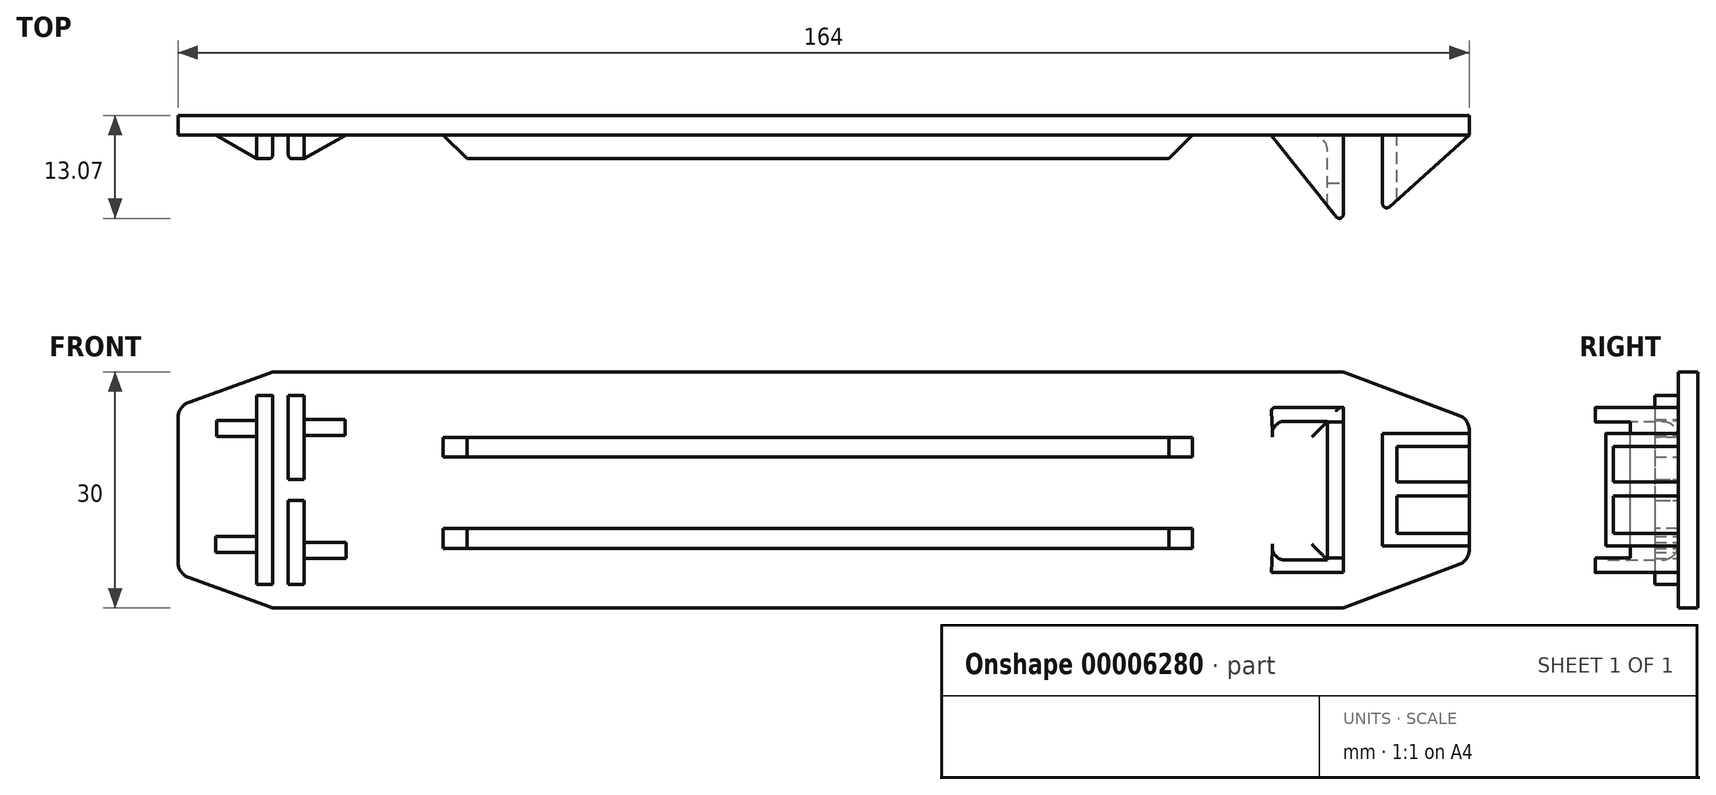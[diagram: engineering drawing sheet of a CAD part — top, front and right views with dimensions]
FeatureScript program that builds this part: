
annotation { "Feature Type Name" : "Feature", "Feature Type Description" : "" }
export const myFeature = defineFeature(function(context is Context, id is Id, definition is map)
    precondition{}
    {
        {
            var Q0;
            Q0=qCreatedBy(makeId("Front.planeOp"),FACE);
            var sketch = newSketch(context, id + "F0", { "sketchPlane" : qUnion([Q0])});
            skLineSegment(sketch, "E0.rect.bottom", {"start": v(66, -15) * mm, "end": v(-70, -15) * mm});
            skLineSegment(sketch, "E0.rect.top", {"start": v(66, 15) * mm, "end": v(-70, 15) * mm});
            skLineSegment(sketch, "E0.rect.left", {"start": v(82, -9) * mm, "end": v(82, 9) * mm});
            skLineSegment(sketch, "E0.rect.right", {"start": v(-82, -10.63) * mm, "end": v(-82, 10.63) * mm});
            skPoint(sketch, "E0.rect.middle", {"position": v(0, 0) * mm});
            skLineSegment(sketch, "E1", {"start": v(66, 15) * mm, "end": v(66, -9.93) * mm, "construction": true});
            skLineSegment(sketch, "E2.rect.bottom", {"start": v(77.85, 9) * mm, "end": v(71, 9) * mm, "construction": true});
            skLineSegment(sketch, "E2.rect.top", {"start": v(77.85, -9) * mm, "end": v(71, -9) * mm, "construction": true});
            skLineSegment(sketch, "E2.rect.left", {"start": v(82, 9) * mm, "end": v(82, -9) * mm, "construction": true});
            skLineSegment(sketch, "E2.rect.right", {"start": v(71, 9) * mm, "end": v(71, -9) * mm, "construction": true});
            skPoint(sketch, "E2.rect.middle", {"position": v(76.5, 0) * mm});
            skLineSegment(sketch, "E3", {"start": v(82, 9) * mm, "end": v(66, 15) * mm});
            skLineSegment(sketch, "E4", {"start": v(82, -9) * mm, "end": v(66, -15) * mm});
            skPoint(sketch, "E5.orphan", {"position": v(82, 15) * mm});
            skPoint(sketch, "E6.orphan", {"position": v(82, -15) * mm});
            skLineSegment(sketch, "E7.rect.bottom", {"start": v(66, 10.5) * mm, "end": v(77.85, 10.5) * mm, "construction": true});
            skLineSegment(sketch, "E7.rect.top", {"start": v(66, -10.5) * mm, "end": v(77.85, -10.5) * mm, "construction": true});
            skLineSegment(sketch, "E7.rect.left", {"start": v(66, 10.5) * mm, "end": v(66, -10.5) * mm, "construction": true});
            skLineSegment(sketch, "E7.rect.right", {"start": v(77.85, 10.5) * mm, "end": v(77.85, -10.5) * mm, "construction": true});
            skPoint(sketch, "E7.rect.middle", {"position": v(71.92, 0) * mm});
            skLineSegment(sketch, "E8.bottom", {"start": v(66, 10.5) * mm, "end": v(56.87, 10.5) * mm});
            skLineSegment(sketch, "E8.top", {"start": v(66, -10.5) * mm, "end": v(56.87, -10.5) * mm});
            skLineSegment(sketch, "E8.left", {"start": v(66, 10.5) * mm, "end": v(66, -10.5) * mm});
            skLineSegment(sketch, "E9.bottom", {"start": v(64, 8.72) * mm, "end": v(56.94, 8.72) * mm});
            skLineSegment(sketch, "E9.top", {"start": v(64, -8.88) * mm, "end": v(56.94, -8.88) * mm});
            skLineSegment(sketch, "E9.left", {"start": v(66, 8.72) * mm, "end": v(66, -8.88) * mm});
            skLineSegment(sketch, "E10", {"start": v(56.87, 10.5) * mm, "end": v(56.94, 8.72) * mm});
            skLineSegment(sketch, "E11", {"start": v(56.94, -8.88) * mm, "end": v(56.87, -10.5) * mm});
            skLineSegment(sketch, "E12", {"start": v(64, 8.72) * mm, "end": v(64, -8.88) * mm});
            skLineSegment(sketch, "E13", {"start": v(71, -9) * mm, "end": v(71, 9) * mm});
            skLineSegment(sketch, "E14", {"start": v(71, 7.5) * mm, "end": v(77.85, 7.5) * mm});
            skLineSegment(sketch, "E15", {"start": v(71, -7.5) * mm, "end": v(77.85, -7.5) * mm});
            skLineSegment(sketch, "E16.bottom", {"start": v(72.8, 5.5) * mm, "end": v(82, 5.5) * mm});
            skLineSegment(sketch, "E16.top", {"start": v(72.8, -5.5) * mm, "end": v(82, -5.5) * mm});
            skLineSegment(sketch, "E16.left", {"start": v(72.8, 5.5) * mm, "end": v(72.8, 1.01) * mm});
            skLineSegment(sketch, "E16.right", {"start": v(82, 5.5) * mm, "end": v(82, -5.5) * mm});
            skLineSegment(sketch, "E17.bottom", {"start": v(72.8, 1.01) * mm, "end": v(82, 1.01) * mm});
            skLineSegment(sketch, "E17.top", {"start": v(72.8, -0.79) * mm, "end": v(82, -0.79) * mm});
            skLineSegment(sketch, "E17.right", {"start": v(82, 1.01) * mm, "end": v(82, -0.79) * mm});
            skLineSegment(sketch, "E18.trimOffspring", {"start": v(72.8, -0.79) * mm, "end": v(72.8, -5.5) * mm});
            skLineSegment(sketch, "E19", {"start": v(71, 7.15) * mm, "end": v(82, 7.15) * mm});
            skLineSegment(sketch, "E20", {"start": v(71, -7.11) * mm, "end": v(82, -7.11) * mm});
            skLineSegment(sketch, "E21", {"start": v(82, -7.11) * mm, "end": v(81.8, -7.11) * mm});
            skLineSegment(sketch, "E22", {"start": v(-70, 3.24) * mm, "end": v(-70, -5.11) * mm, "construction": true});
            skLineSegment(sketch, "E23.rect.bottom", {"start": v(-70, 10.63) * mm, "end": v(-82, 10.63) * mm, "construction": true});
            skLineSegment(sketch, "E23.rect.top", {"start": v(-70, -10.63) * mm, "end": v(-82, -10.63) * mm, "construction": true});
            skLineSegment(sketch, "E23.rect.left", {"start": v(-70, 15) * mm, "end": v(-70, -15) * mm, "construction": true});
            skLineSegment(sketch, "E23.rect.right", {"start": v(-81.6, 10.63) * mm, "end": v(-81.6, -10.63) * mm, "construction": true});
            skPoint(sketch, "E23.rect.middle", {"position": v(-75.8, 0) * mm});
            skLineSegment(sketch, "E24", {"start": v(-82, 10.63) * mm, "end": v(-70, 15) * mm});
            skLineSegment(sketch, "E25", {"start": v(-70, -15) * mm, "end": v(-82, -10.63) * mm});
            skPoint(sketch, "E26.orphan", {"position": v(-82, 15) * mm});
            skPoint(sketch, "E27.orphan", {"position": v(-82, -15) * mm});
            skLineSegment(sketch, "E28.rect.bottom", {"start": v(-70, 12) * mm, "end": v(-72, 12) * mm});
            skLineSegment(sketch, "E28.rect.top", {"start": v(-70, -12) * mm, "end": v(-72, -12) * mm});
            skLineSegment(sketch, "E28.rect.right", {"start": v(-72, 12) * mm, "end": v(-72, -12) * mm});
            skPoint(sketch, "E28.rect.middle", {"position": v(-70, 0) * mm});
            skPoint(sketch, "E28.rect.left.start.orphan", {"position": v(-68, 12) * mm});
            skPoint(sketch, "E29.orphan", {"position": v(-68, -12) * mm});
            skLineSegment(sketch, "E30", {"start": v(-70, 12) * mm, "end": v(-70, -12) * mm});
            skLineSegment(sketch, "E31.rect.bottom", {"start": v(-66, 12) * mm, "end": v(-68, 12) * mm});
            skLineSegment(sketch, "E31.rect.top", {"start": v(-66, -12) * mm, "end": v(-68, -12) * mm});
            skLineSegment(sketch, "E31.rect.left", {"start": v(-66, 12) * mm, "end": v(-66, 1.35) * mm});
            skLineSegment(sketch, "E31.rect.right", {"start": v(-68, 12) * mm, "end": v(-68, 1.35) * mm});
            skPoint(sketch, "E31.rect.middle", {"position": v(-67, 0) * mm});
            skLineSegment(sketch, "E32.rect.bottom", {"start": v(-66, 1.35) * mm, "end": v(-68, 1.35) * mm});
            skLineSegment(sketch, "E32.rect.top", {"start": v(-66, -1.35) * mm, "end": v(-68, -1.35) * mm});
            skLineSegment(sketch, "E33.trimOffspring", {"start": v(-68, -1.35) * mm, "end": v(-68, -12) * mm});
            skLineSegment(sketch, "E34.trimOffspring", {"start": v(-66, -1.35) * mm, "end": v(-66, -12) * mm});
            skLineSegment(sketch, "E35.bottom", {"start": v(-66, 8.93) * mm, "end": v(-60.79, 8.93) * mm});
            skLineSegment(sketch, "E35.top", {"start": v(-66, 6.93) * mm, "end": v(-60.79, 6.93) * mm});
            skLineSegment(sketch, "E35.left", {"start": v(-66, 8.93) * mm, "end": v(-66, 6.93) * mm});
            skLineSegment(sketch, "E35.right", {"start": v(-60.79, 8.93) * mm, "end": v(-60.79, 6.93) * mm});
            skLineSegment(sketch, "E36.bottom", {"start": v(-66, -6.68) * mm, "end": v(-60.7, -6.68) * mm});
            skLineSegment(sketch, "E36.top", {"start": v(-66, -8.68) * mm, "end": v(-60.7, -8.68) * mm});
            skLineSegment(sketch, "E36.left", {"start": v(-66, -6.68) * mm, "end": v(-66, -8.68) * mm});
            skLineSegment(sketch, "E36.right", {"start": v(-60.7, -6.68) * mm, "end": v(-60.7, -8.68) * mm});
            skLineSegment(sketch, "E37.bottom", {"start": v(-72, 8.8) * mm, "end": v(-77.12, 8.8) * mm});
            skLineSegment(sketch, "E37.top", {"start": v(-72, 6.8) * mm, "end": v(-77.12, 6.8) * mm});
            skLineSegment(sketch, "E37.left", {"start": v(-72, 8.8) * mm, "end": v(-72, 6.8) * mm});
            skLineSegment(sketch, "E37.right", {"start": v(-77.12, 8.8) * mm, "end": v(-77.12, 6.8) * mm});
            skLineSegment(sketch, "E38.bottom", {"start": v(-72, -5.93) * mm, "end": v(-77.26, -5.93) * mm});
            skLineSegment(sketch, "E38.top", {"start": v(-72, -7.93) * mm, "end": v(-77.26, -7.93) * mm});
            skLineSegment(sketch, "E38.left", {"start": v(-72, -5.93) * mm, "end": v(-72, -7.93) * mm});
            skLineSegment(sketch, "E38.right", {"start": v(-77.26, -5.93) * mm, "end": v(-77.26, -7.93) * mm});
            skSolve(sketch);
        }
        {
            var Q0;
            {var subQ2=sQuery(id+"F0.wireOp",EDGE,"E31.rect.top");Q0=makeQuery(id+"F0.imprint","IMPRINT",FACE,{"disambiguationData":[TD([[makeQuery(id+"F0.imprint","IMPRINT",EDGE,{"derivedFrom":subQ2}),-1.0]])]});}
            var Q1;
            {var subQ3=sQuery(id+"F0.wireOp",EDGE,"E8.bottom");Q1=makeQuery(id+"F0.imprint","IMPRINT",FACE,{"disambiguationData":[TD([[makeQuery(id+"F0.imprint","IMPRINT",EDGE,{"derivedFrom":subQ3}),1.0]])]});}
            var Q2;
            {var subQ2=sQuery(id+"F0.wireOp",EDGE,"E16.top");Q2=makeQuery(id+"F0.imprint","IMPRINT",FACE,{"disambiguationData":[TD([[makeQuery(id+"F0.imprint","IMPRINT",EDGE,{"derivedFrom":subQ2}),1.0]])]});}
            var Q3;
            {var subQ4=sQuery(id+"F0.wireOp",EDGE,"E16.bottom");Q3=makeQuery(id+"F0.imprint","IMPRINT",FACE,{"disambiguationData":[TD([[makeQuery(id+"F0.imprint","IMPRINT",EDGE,{"derivedFrom":subQ4}),1.0]])]});}
            var Q4;
            {var subQ3=sQuery(id+"F0.wireOp",EDGE,"E31.rect.bottom");Q4=makeQuery(id+"F0.imprint","IMPRINT",FACE,{"disambiguationData":[TD([[makeQuery(id+"F0.imprint","IMPRINT",EDGE,{"derivedFrom":subQ3}),1.0]])]});}
            var Q5;
            Q5=makeQuery(id+"F0.imprint","IMPRINT",FACE,{"disambiguationData":[TD([[makeQuery(id+"F0.imprint","IMPRINT",EDGE,{"derivedFrom":sQuery(id+"F0.wireOp",EDGE,"E35.bottom")}),-1.0]])]});
            var Q6;
            {var subQ2=sQuery(id+"F0.wireOp",EDGE,"E16.bottom");Q6=makeQuery(id+"F0.imprint","IMPRINT",FACE,{"disambiguationData":[TD([[makeQuery(id+"F0.imprint","IMPRINT",EDGE,{"derivedFrom":subQ2}),-1.0]])]});}
            var Q7;
            Q7=makeQuery(id+"F0.imprint","IMPRINT",FACE,{"disambiguationData":[TD([[makeQuery(id+"F0.imprint","IMPRINT",EDGE,{"derivedFrom":sQuery(id+"F0.wireOp",EDGE,"E0.rect.bottom")}),-1.0]])]});
            var Q8;
            {var subQ4=sQuery(id+"F0.wireOp",EDGE,"E28.rect.bottom");Q8=makeQuery(id+"F0.imprint","IMPRINT",FACE,{"disambiguationData":[TD([[makeQuery(id+"F0.imprint","IMPRINT",EDGE,{"derivedFrom":subQ4}),1.0]])]});}
            var Q9;
            Q9=makeQuery(id+"F0.imprint","IMPRINT",FACE,{"disambiguationData":[TD([[makeQuery(id+"F0.imprint","IMPRINT",EDGE,{"derivedFrom":sQuery(id+"F0.wireOp",EDGE,"E38.bottom")}),1.0]])]});
            var Q10;
            Q10=makeQuery(id+"F0.imprint","IMPRINT",FACE,{"disambiguationData":[TD([[makeQuery(id+"F0.imprint","IMPRINT",EDGE,{"derivedFrom":sQuery(id+"F0.wireOp",EDGE,"E37.bottom")}),1.0]])]});
            var Q11;
            Q11=makeQuery(id+"F0.imprint","IMPRINT",FACE,{"disambiguationData":[TD([[makeQuery(id+"F0.imprint","IMPRINT",EDGE,{"derivedFrom":sQuery(id+"F0.wireOp",EDGE,"E36.bottom")}),-1.0]])]});
            extrude(context, id + "F1", {"entities" : qUnion([Q0, Q1, Q2, Q3, Q4, Q5, Q6, Q7, Q8, Q9, Q10, Q11]), "depth" : 2.5 * mm});
        }
        {
            var Q0;
            {var subQ2=sQuery(id+"F0.wireOp",EDGE,"E31.rect.top");Q0=makeQuery(id+"F0.imprint","IMPRINT",FACE,{"disambiguationData":[TD([[makeQuery(id+"F0.imprint","IMPRINT",EDGE,{"derivedFrom":subQ2}),-1.0]])]});}
            var Q1;
            {var subQ3=sQuery(id+"F0.wireOp",EDGE,"E31.rect.bottom");Q1=makeQuery(id+"F0.imprint","IMPRINT",FACE,{"disambiguationData":[TD([[makeQuery(id+"F0.imprint","IMPRINT",EDGE,{"derivedFrom":subQ3}),1.0]])]});}
            var Q2;
            Q2=makeQuery(id+"F0.imprint","IMPRINT",FACE,{"disambiguationData":[TD([[makeQuery(id+"F0.imprint","IMPRINT",EDGE,{"derivedFrom":sQuery(id+"F0.wireOp",EDGE,"E35.bottom")}),-1.0]])]});
            var Q3;
            Q3=makeQuery(id+"F0.imprint","IMPRINT",FACE,{"disambiguationData":[TD([[makeQuery(id+"F0.imprint","IMPRINT",EDGE,{"derivedFrom":sQuery(id+"F0.wireOp",EDGE,"E36.bottom")}),-1.0]])]});
            var Q4;
            {var subQ4=sQuery(id+"F0.wireOp",EDGE,"E28.rect.bottom");Q4=makeQuery(id+"F0.imprint","IMPRINT",FACE,{"disambiguationData":[TD([[makeQuery(id+"F0.imprint","IMPRINT",EDGE,{"derivedFrom":subQ4}),1.0]])]});}
            var Q5;
            Q5=makeQuery(id+"F0.imprint","IMPRINT",FACE,{"disambiguationData":[TD([[makeQuery(id+"F0.imprint","IMPRINT",EDGE,{"derivedFrom":sQuery(id+"F0.wireOp",EDGE,"E38.bottom")}),1.0]])]});
            var Q6;
            Q6=makeQuery(id+"F0.imprint","IMPRINT",FACE,{"disambiguationData":[TD([[makeQuery(id+"F0.imprint","IMPRINT",EDGE,{"derivedFrom":sQuery(id+"F0.wireOp",EDGE,"E37.bottom")}),1.0]])]});
            extrude(context, id + "F2", {"entities" : qUnion([Q0, Q1, Q2, Q3, Q4, Q5, Q6]), "operationType" : NewBodyOperationType.ADD, "depth" : 5.5 * mm});
        }
        {
            var Q0;
            {var subQ4=sQuery(id+"F0.wireOp",EDGE,"E16.bottom");Q0=makeQuery(id+"F0.imprint","IMPRINT",FACE,{"disambiguationData":[TD([[makeQuery(id+"F0.imprint","IMPRINT",EDGE,{"derivedFrom":subQ4}),1.0]])]});}
            extrude(context, id + "F3", {"entities" : qUnion([Q0]), "operationType" : NewBodyOperationType.ADD, "depth" : 12.35 * mm});
        }
        {
            var Q0;
            {var subQ3=sQuery(id+"F0.wireOp",EDGE,"E8.bottom");Q0=makeQuery(id+"F0.imprint","IMPRINT",FACE,{"disambiguationData":[TD([[makeQuery(id+"F0.imprint","IMPRINT",EDGE,{"derivedFrom":subQ3}),1.0]])]});}
            extrude(context, id + "F4", {"entities" : qUnion([Q0]), "operationType" : NewBodyOperationType.ADD, "depth" : 14 * mm});
        }
        {
            var Q0;
            Q0=makeQuery(id+"F4.opExtrude","SWEPT_FACE",FACE,{"disambiguationData":[OSD([sQuery(id+"F0.wireOp",EDGE,"E8.top")])]});
            var sketch = newSketch(context, id + "F5", { "sketchPlane" : qUnion([Q0])});
            skLineSegment(sketch, "E39", {"start": v(66, 14) * mm, "end": v(56.87, 2.5) * mm});
            skSolve(sketch);
        }
        {
            var Q0;
            Q0=makeQuery(id+"F5.imprint","IMPRINT",FACE,{"disambiguationData":[TD([[makeQuery(id+"F5.imprint","IMPRINT",EDGE,{"derivedFrom":sQuery(id+"F5.wireOp",EDGE,"E39")}),-1.0]])]});
            extrude(context, id + "F6", {"entities" : qUnion([Q0]), "operationType" : NewBodyOperationType.REMOVE, "endBound" : BoundingType.THROUGH_ALL, "oppositeDirection" : true, "depth" : 25 * mm});
        }
        {
            var Q0;
            Q0=makeQuery(id+"F3.opExtrude","SWEPT_FACE",FACE,{"disambiguationData":[OSD([sQuery(id+"F0.wireOp",EDGE,"E20"),sQuery(id+"F0.wireOp",EDGE,"E21")])]});
            var sketch = newSketch(context, id + "F7", { "sketchPlane" : qUnion([Q0])});
            skLineSegment(sketch, "E40", {"start": v(71, 12.35) * mm, "end": v(82, 2.5) * mm});
            skSolve(sketch);
        }
        {
            var Q0;
            Q0=makeQuery(id+"F7.imprint","IMPRINT",FACE,{"disambiguationData":[TD([[makeQuery(id+"F7.imprint","IMPRINT",EDGE,{"derivedFrom":sQuery(id+"F7.wireOp",EDGE,"E40")}),1.0]])]});
            extrude(context, id + "F8", {"entities" : qUnion([Q0]), "operationType" : NewBodyOperationType.REMOVE, "endBound" : BoundingType.THROUGH_ALL, "oppositeDirection" : true, "depth" : 25 * mm});
        }
        {
            var Q0;
            Q0=makeQuery(id+"F4.opExtrude","SWEPT_FACE",FACE,{"disambiguationData":[OSD([sQuery(id+"F0.wireOp",EDGE,"E8.left"),sQuery(id+"F0.wireOp",EDGE,"E9.left")])]});
            var sketch = newSketch(context, id + "F9", { "sketchPlane" : qUnion([Q0])});
            skLineSegment(sketch, "E41.bottom", {"start": v(-14, -8.65) * mm, "end": v(-8.6, -8.65) * mm});
            skLineSegment(sketch, "E41.top", {"start": v(-14, 8.65) * mm, "end": v(-8.6, 8.65) * mm});
            skLineSegment(sketch, "E41.left", {"start": v(-14, -8.65) * mm, "end": v(-14, 8.65) * mm});
            skLineSegment(sketch, "E41.right", {"start": v(-8.6, -8.65) * mm, "end": v(-8.6, 8.65) * mm});
            skSolve(sketch);
        }
        {
            var Q0;
            Q0=makeQuery(id+"F9.imprint","IMPRINT",FACE,{"disambiguationData":[TD([[makeQuery(id+"F9.imprint","IMPRINT",EDGE,{"derivedFrom":sQuery(id+"F9.wireOp",EDGE,"E41.bottom")}),1.0]])]});
            extrude(context, id + "F10", {"entities" : qUnion([Q0]), "operationType" : NewBodyOperationType.REMOVE, "oppositeDirection" : true, "depth" : 25 * mm});
        }
        {
            var Q0;
            Q0=makeQuery(id+"F2.opExtrude","SWEPT_FACE",FACE,{"disambiguationData":[OSD([sQuery(id+"F0.wireOp",EDGE,"E38.top")])]});
            var sketch = newSketch(context, id + "F11", { "sketchPlane" : qUnion([Q0])});
            skLineSegment(sketch, "E42", {"start": v(-72, 5.5) * mm, "end": v(-77.26, 2.5) * mm});
            skSolve(sketch);
        }
        {
            var Q0;
            Q0=makeQuery(id+"F11.imprint","IMPRINT",FACE,{"disambiguationData":[TD([[makeQuery(id+"F11.imprint","IMPRINT",EDGE,{"derivedFrom":sQuery(id+"F11.wireOp",EDGE,"E42")}),-1.0]])]});
            extrude(context, id + "F12", {"entities" : qUnion([Q0]), "operationType" : NewBodyOperationType.REMOVE, "oppositeDirection" : true, "depth" : 25 * mm});
        }
        {
            var Q0;
            Q0=makeQuery(id+"F2.opExtrude","SWEPT_FACE",FACE,{"disambiguationData":[OSD([sQuery(id+"F0.wireOp",EDGE,"E36.top")])]});
            var sketch = newSketch(context, id + "F13", { "sketchPlane" : qUnion([Q0])});
            skLineSegment(sketch, "E43", {"start": v(-60.7, 2.5) * mm, "end": v(-66, 5.5) * mm});
            skSolve(sketch);
        }
        {
            var Q0;
            Q0=makeQuery(id+"F13.imprint","IMPRINT",FACE,{"disambiguationData":[TD([[makeQuery(id+"F13.imprint","IMPRINT",EDGE,{"derivedFrom":sQuery(id+"F13.wireOp",EDGE,"E43")}),-1.0]])]});
            extrude(context, id + "F14", {"entities" : qUnion([Q0]), "operationType" : NewBodyOperationType.REMOVE, "oppositeDirection" : true, "depth" : 25 * mm});
        }
        {
            var Q0;
            Q0=makeQuery(id+"F2.opExtrude","CAP_EDGE",EDGE,{"disambiguationData":[OSD([sQuery(id+"F0.wireOp",EDGE,"E30")])],"isStart":false});
            var Q1;
            Q1=makeQuery(id+"F2.opExtrude","CAP_EDGE",EDGE,{"disambiguationData":[OSD([sQuery(id+"F0.wireOp",EDGE,"E33.trimOffspring")])],"isStart":false});
            var Q2;
            Q2=makeQuery(id+"F2.opExtrude","CAP_EDGE",EDGE,{"disambiguationData":[OSD([sQuery(id+"F0.wireOp",EDGE,"E31.rect.right")])],"isStart":false});
            var Q3;
            Q3=makeQuery(id+"F6.boolean.opBoolean","COPY",EDGE,{"derivedFrom":makeQuery(id+"F6.opExtrude","CAP_EDGE",EDGE,{"disambiguationData":[OSD([sQuery(id+"F5.wireOp",EDGE,"E39")])],"isStart":true})});
            var Q4;
            Q4=makeQuery(id+"F6.boolean.opBoolean","INTERSECT",EDGE,{"derivedFrom":[makeQuery(id+"F4.opExtrude","SWEPT_FACE",FACE,{"disambiguationData":[OSD([sQuery(id+"F0.wireOp",EDGE,"E8.bottom")])]}),makeQuery(id+"F6.opExtrude","SWEPT_FACE",FACE,{"disambiguationData":[OSD([sQuery(id+"F5.wireOp",EDGE,"E39")])]})]});
            var Q5;
            {var subQ0=sQuery(id+"F0.wireOp",EDGE,"E13");Q5=makeQuery(id+"F8.boolean.opBoolean","MERGE",EDGE,{"derivedFrom":[makeQuery(id+"F3.opExtrude","CAP_EDGE",EDGE,{"disambiguationData":[OSD([subQ0])],"isStart":false}),makeQuery(id+"F8.opExtrude","SWEPT_EDGE",EDGE,{"disambiguationData":[OSD([subQ0,sQuery(id+"F0.wireOp",EDGE,"E20"),sQuery(id+"F0.wireOp",EDGE,"E21"),sQuery(id+"F7.wireOp",EDGE,"E40")])]})]});}
            var Q6;
            {var subQ0=sQuery(id+"F0.wireOp",EDGE,"E8.left");var subQ1=sQuery(id+"F0.wireOp",EDGE,"E9.left");var subQ2=sQuery(id+"F0.wireOp",EDGE,"E8.top");var subQ3=sQuery(id+"F5.wireOp",EDGE,"E39");Q6=makeQuery(id+"F10.boolean.opBoolean","SPLIT",EDGE,{"disambiguationData":[TD([makeQuery(id+"F4.opExtrude","SWEPT_FACE",FACE,{"disambiguationData":[OSD([subQ2])]})])],"derivedFrom":makeQuery(id+"F6.boolean.opBoolean","MERGE",EDGE,{"derivedFrom":[makeQuery(id+"F4.opExtrude","CAP_EDGE",EDGE,{"disambiguationData":[OSD([subQ0,subQ1])],"isStart":false}),makeQuery(id+"F6.opExtrude","SWEPT_EDGE",EDGE,{"disambiguationData":[OSD([subQ2,subQ0,subQ3])]})]})});}
            var Q7;
            {var subQ0=sQuery(id+"F0.wireOp",EDGE,"E8.left");var subQ1=sQuery(id+"F0.wireOp",EDGE,"E9.left");var subQ2=sQuery(id+"F5.wireOp",EDGE,"E39");Q7=makeQuery(id+"F10.boolean.opBoolean","SPLIT",EDGE,{"disambiguationData":[TD([makeQuery(id+"F4.opExtrude","SWEPT_FACE",FACE,{"disambiguationData":[OSD([sQuery(id+"F0.wireOp",EDGE,"E8.bottom")])]})])],"derivedFrom":makeQuery(id+"F6.boolean.opBoolean","MERGE",EDGE,{"derivedFrom":[makeQuery(id+"F4.opExtrude","CAP_EDGE",EDGE,{"disambiguationData":[OSD([subQ0,subQ1])],"isStart":false}),makeQuery(id+"F6.opExtrude","SWEPT_EDGE",EDGE,{"disambiguationData":[OSD([sQuery(id+"F0.wireOp",EDGE,"E8.top"),subQ0,subQ2])]})]})});}
            fillet(context, id + "F15", {"entities" : qUnion([Q0, Q1, Q2, Q3, Q4, Q5, Q6, Q7]), "radius" : .5 * mm, "tangentPropagation" : true, "allowEdgeOverflow" : false});
        }
        {
            var Q0;
            {var subQ0=sQuery(id+"F0.wireOp",EDGE,"E0.rect.bottom");var subQ1=sQuery(id+"F0.wireOp",EDGE,"E0.rect.top");var subQ2=sQuery(id+"F0.wireOp",EDGE,"E0.rect.left");var subQ3=sQuery(id+"F0.wireOp",EDGE,"E0.rect.right");var subQ4=sQuery(id+"F0.wireOp",EDGE,"E3");var subQ5=sQuery(id+"F0.wireOp",EDGE,"E4");var subQ6=sQuery(id+"F0.wireOp",EDGE,"E16.right");var subQ7=sQuery(id+"F0.wireOp",EDGE,"E17.right");var subQ8=sQuery(id+"F0.wireOp",EDGE,"E24");var subQ9=sQuery(id+"F0.wireOp",EDGE,"E25");Q0=makeQuery(id+"F4.boolean.opBoolean","INTERSECT",EDGE,{"derivedFrom":[makeQuery(id+"F3.boolean.opBoolean","SPLIT",FACE,{"disambiguationData":[TD([makeQuery(id+"F1.opExtrude","SWEPT_FACE",FACE,{"disambiguationData":[OSD([subQ0])]})])],"derivedFrom":makeQuery(id+"F1.opExtrude","CAP_FACE",FACE,{"disambiguationData":[OSD([subQ0,subQ1,subQ2,subQ3,subQ4,subQ5,subQ6,subQ7,subQ8,subQ9])],"isStart":false})}),makeQuery(id+"F4.opExtrude","SWEPT_FACE",FACE,{"disambiguationData":[OSD([sQuery(id+"F0.wireOp",EDGE,"E12")])]})]});}
            var Q1;
            {var subQ0=sQuery(id+"F0.wireOp",EDGE,"E0.rect.bottom");var subQ1=sQuery(id+"F0.wireOp",EDGE,"E0.rect.top");var subQ2=sQuery(id+"F0.wireOp",EDGE,"E0.rect.left");var subQ3=sQuery(id+"F0.wireOp",EDGE,"E0.rect.right");var subQ4=sQuery(id+"F0.wireOp",EDGE,"E3");var subQ5=sQuery(id+"F0.wireOp",EDGE,"E4");var subQ6=sQuery(id+"F0.wireOp",EDGE,"E16.right");var subQ7=sQuery(id+"F0.wireOp",EDGE,"E17.right");var subQ8=sQuery(id+"F0.wireOp",EDGE,"E24");var subQ9=sQuery(id+"F0.wireOp",EDGE,"E25");Q1=makeQuery(id+"F4.boolean.opBoolean","INTERSECT",EDGE,{"derivedFrom":[makeQuery(id+"F3.boolean.opBoolean","SPLIT",FACE,{"disambiguationData":[TD([makeQuery(id+"F1.opExtrude","SWEPT_FACE",FACE,{"disambiguationData":[OSD([subQ0])]})])],"derivedFrom":makeQuery(id+"F1.opExtrude","CAP_FACE",FACE,{"disambiguationData":[OSD([subQ0,subQ1,subQ2,subQ3,subQ4,subQ5,subQ6,subQ7,subQ8,subQ9])],"isStart":false})}),makeQuery(id+"F4.opExtrude","SWEPT_FACE",FACE,{"disambiguationData":[OSD([sQuery(id+"F0.wireOp",EDGE,"E9.bottom")])]})]});}
            var Q2;
            {var subQ0=sQuery(id+"F0.wireOp",EDGE,"E0.rect.bottom");var subQ1=sQuery(id+"F0.wireOp",EDGE,"E0.rect.top");var subQ2=sQuery(id+"F0.wireOp",EDGE,"E0.rect.left");var subQ3=sQuery(id+"F0.wireOp",EDGE,"E0.rect.right");var subQ4=sQuery(id+"F0.wireOp",EDGE,"E3");var subQ5=sQuery(id+"F0.wireOp",EDGE,"E4");var subQ6=sQuery(id+"F0.wireOp",EDGE,"E16.right");var subQ7=sQuery(id+"F0.wireOp",EDGE,"E17.right");var subQ8=sQuery(id+"F0.wireOp",EDGE,"E24");var subQ9=sQuery(id+"F0.wireOp",EDGE,"E25");Q2=makeQuery(id+"F4.boolean.opBoolean","INTERSECT",EDGE,{"derivedFrom":[makeQuery(id+"F3.boolean.opBoolean","SPLIT",FACE,{"disambiguationData":[TD([makeQuery(id+"F1.opExtrude","SWEPT_FACE",FACE,{"disambiguationData":[OSD([subQ0])]})])],"derivedFrom":makeQuery(id+"F1.opExtrude","CAP_FACE",FACE,{"disambiguationData":[OSD([subQ0,subQ1,subQ2,subQ3,subQ4,subQ5,subQ6,subQ7,subQ8,subQ9])],"isStart":false})}),makeQuery(id+"F4.opExtrude","SWEPT_FACE",FACE,{"disambiguationData":[OSD([sQuery(id+"F0.wireOp",EDGE,"E9.top")])]})]});}
            fillet(context, id + "F16", {"entities" : qUnion([Q0, Q1, Q2]), "radius" : 2 * mm, "tangentPropagation" : true, "allowEdgeOverflow" : false});
        }
        {
            var Q0;
            {var subQ0=sQuery(id+"F0.wireOp",EDGE,"E0.rect.bottom");var subQ1=sQuery(id+"F0.wireOp",EDGE,"E0.rect.top");var subQ2=sQuery(id+"F0.wireOp",EDGE,"E0.rect.left");var subQ3=sQuery(id+"F0.wireOp",EDGE,"E0.rect.right");var subQ4=sQuery(id+"F0.wireOp",EDGE,"E3");var subQ5=sQuery(id+"F0.wireOp",EDGE,"E4");var subQ6=sQuery(id+"F0.wireOp",EDGE,"E16.right");var subQ7=sQuery(id+"F0.wireOp",EDGE,"E17.right");var subQ8=sQuery(id+"F0.wireOp",EDGE,"E24");var subQ9=sQuery(id+"F0.wireOp",EDGE,"E25");Q0=makeQuery(id+"F3.boolean.opBoolean","SPLIT",FACE,{"disambiguationData":[TD([makeQuery(id+"F1.opExtrude","SWEPT_FACE",FACE,{"disambiguationData":[OSD([subQ0])]})])],"derivedFrom":makeQuery(id+"F1.opExtrude","CAP_FACE",FACE,{"disambiguationData":[OSD([subQ0,subQ1,subQ2,subQ3,subQ4,subQ5,subQ6,subQ7,subQ8,subQ9])],"isStart":false})});}
            var sketch = newSketch(context, id + "F17", { "sketchPlane" : qUnion([Q0])});
            skLineSegment(sketch, "E44.bottom", {"start": v(-48.32, 6.69) * mm, "end": v(46.86, 6.69) * mm});
            skLineSegment(sketch, "E44.top", {"start": v(-48.32, 4.19) * mm, "end": v(46.86, 4.19) * mm});
            skLineSegment(sketch, "E44.left", {"start": v(-48.32, 6.69) * mm, "end": v(-48.32, 4.19) * mm});
            skLineSegment(sketch, "E44.right", {"start": v(46.86, 6.69) * mm, "end": v(46.86, 4.19) * mm});
            skLineSegment(sketch, "E45.bottom", {"start": v(-48.32, -4.92) * mm, "end": v(46.86, -4.92) * mm});
            skLineSegment(sketch, "E45.top", {"start": v(-48.32, -7.42) * mm, "end": v(46.86, -7.42) * mm});
            skLineSegment(sketch, "E45.left", {"start": v(-48.32, -4.92) * mm, "end": v(-48.32, -7.42) * mm});
            skLineSegment(sketch, "E45.right", {"start": v(46.86, -4.92) * mm, "end": v(46.86, -7.42) * mm});
            skSolve(sketch);
        }
        {
            var Q0;
            Q0=makeQuery(id+"F17.imprint","IMPRINT",FACE,{"disambiguationData":[TD([[makeQuery(id+"F17.imprint","IMPRINT",EDGE,{"derivedFrom":sQuery(id+"F17.wireOp",EDGE,"E44.bottom")}),-1.0]])]});
            var Q1;
            Q1=makeQuery(id+"F17.imprint","IMPRINT",FACE,{"disambiguationData":[TD([[makeQuery(id+"F17.imprint","IMPRINT",EDGE,{"derivedFrom":sQuery(id+"F17.wireOp",EDGE,"E45.bottom")}),-1.0]])]});
            extrude(context, id + "F18", {"entities" : qUnion([Q0, Q1]), "operationType" : NewBodyOperationType.ADD, "depth" : 3 * mm});
        }
        {
            var Q0;
            Q0=makeQuery(id+"F18.opExtrude","CAP_EDGE",EDGE,{"disambiguationData":[OSD([sQuery(id+"F17.wireOp",EDGE,"E45.left")])],"isStart":false});
            var Q1;
            Q1=makeQuery(id+"F18.opExtrude","CAP_EDGE",EDGE,{"disambiguationData":[OSD([sQuery(id+"F17.wireOp",EDGE,"E44.left")])],"isStart":false});
            var Q2;
            Q2=makeQuery(id+"F18.opExtrude","CAP_EDGE",EDGE,{"disambiguationData":[OSD([sQuery(id+"F17.wireOp",EDGE,"E45.right")])],"isStart":false});
            var Q3;
            Q3=makeQuery(id+"F18.opExtrude","CAP_EDGE",EDGE,{"disambiguationData":[OSD([sQuery(id+"F17.wireOp",EDGE,"E44.right")])],"isStart":false});
            chamfer(context, id + "F19", {"entities" : qUnion([Q0, Q1, Q2, Q3]), "width" : 3 * mm, "tangentPropagation" : true});
        }
        {
            var Q0;
            Q0=makeQuery(id+"F1.opExtrude","SWEPT_EDGE",EDGE,{"disambiguationData":[OSD([sQuery(id+"F0.wireOp",EDGE,"E0.rect.right"),sQuery(id+"F0.wireOp",EDGE,"E25")])]});
            var Q1;
            Q1=makeQuery(id+"F1.opExtrude","SWEPT_EDGE",EDGE,{"disambiguationData":[OSD([sQuery(id+"F0.wireOp",EDGE,"E0.rect.bottom"),sQuery(id+"F0.wireOp",EDGE,"E25")])]});
            var Q2;
            Q2=makeQuery(id+"F1.opExtrude","SWEPT_EDGE",EDGE,{"disambiguationData":[OSD([sQuery(id+"F0.wireOp",EDGE,"E0.rect.bottom"),sQuery(id+"F0.wireOp",EDGE,"E4")])]});
            var Q3;
            Q3=makeQuery(id+"F1.opExtrude","SWEPT_EDGE",EDGE,{"disambiguationData":[OSD([sQuery(id+"F0.wireOp",EDGE,"E0.rect.left"),sQuery(id+"F0.wireOp",EDGE,"E4")])]});
            var Q4;
            Q4=makeQuery(id+"F1.opExtrude","SWEPT_EDGE",EDGE,{"disambiguationData":[OSD([sQuery(id+"F0.wireOp",EDGE,"E0.rect.top"),sQuery(id+"F0.wireOp",EDGE,"E24")])]});
            var Q5;
            Q5=makeQuery(id+"F1.opExtrude","SWEPT_EDGE",EDGE,{"disambiguationData":[OSD([sQuery(id+"F0.wireOp",EDGE,"E0.rect.right"),sQuery(id+"F0.wireOp",EDGE,"E24")])]});
            var Q6;
            Q6=makeQuery(id+"F1.opExtrude","SWEPT_EDGE",EDGE,{"disambiguationData":[OSD([sQuery(id+"F0.wireOp",EDGE,"E0.rect.left"),sQuery(id+"F0.wireOp",EDGE,"E3")])]});
            var Q7;
            Q7=makeQuery(id+"F1.opExtrude","SWEPT_EDGE",EDGE,{"disambiguationData":[OSD([sQuery(id+"F0.wireOp",EDGE,"E0.rect.top"),sQuery(id+"F0.wireOp",EDGE,"E3")])]});
            fillet(context, id + "F20", {"entities" : qUnion([Q0, Q1, Q2, Q3, Q4, Q5, Q6, Q7]), "radius" : 2 * mm, "tangentPropagation" : true, "allowEdgeOverflow" : false});
        }
    });
